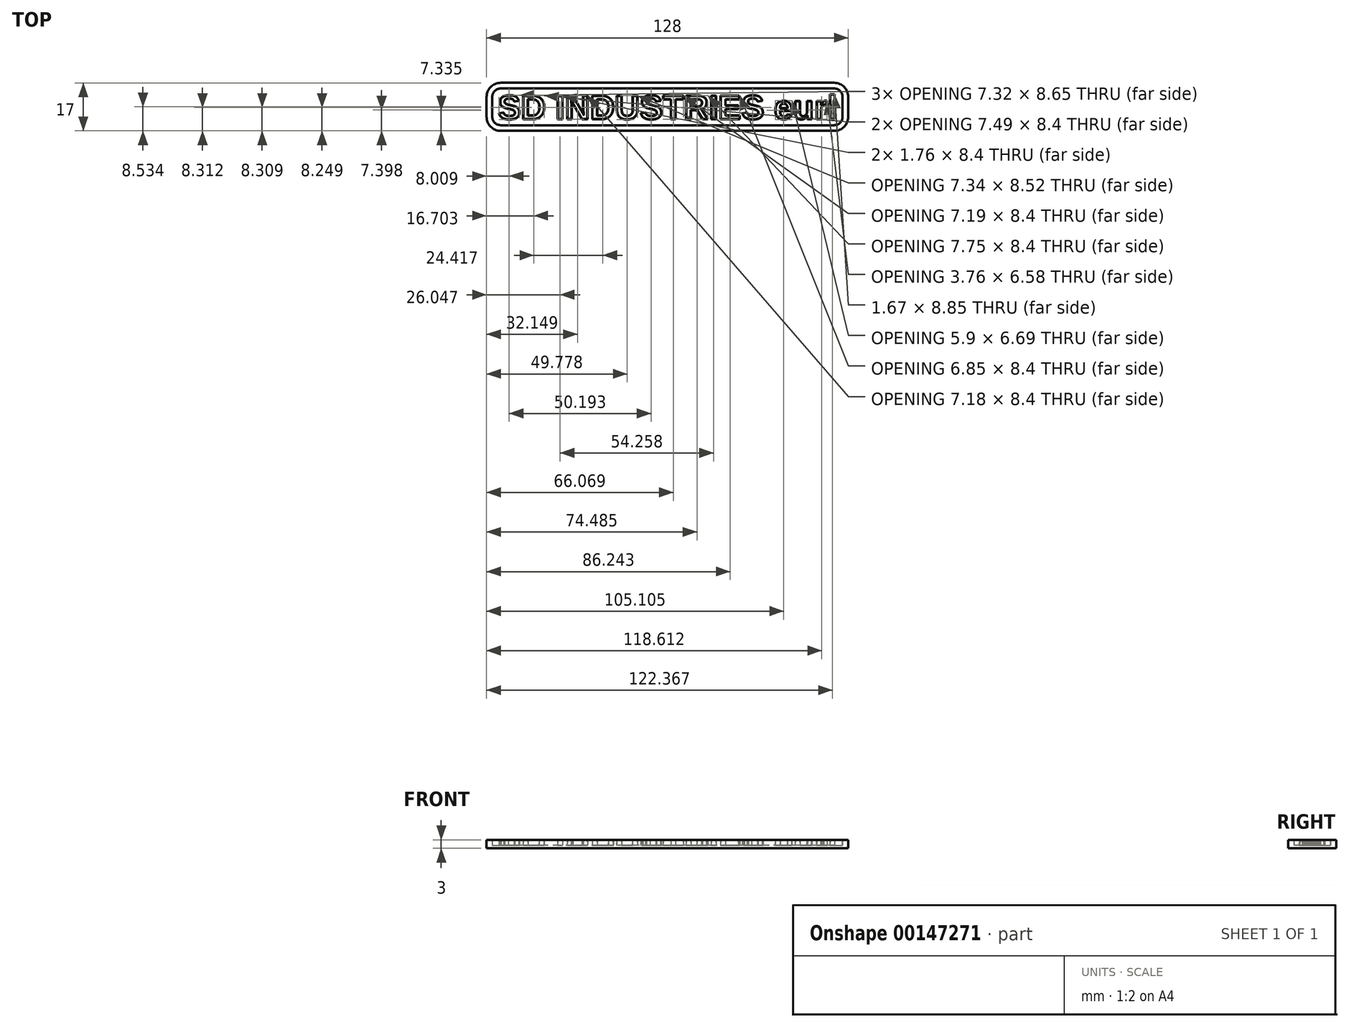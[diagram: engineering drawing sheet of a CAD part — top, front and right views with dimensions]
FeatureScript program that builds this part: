
annotation { "Feature Type Name" : "Feature", "Feature Type Description" : "" }
export const myFeature = defineFeature(function(context is Context, id is Id, definition is map)
    precondition{}
    {
        {
            var Q0;
            Q0=qCreatedBy(makeId("Top.planeOp"),FACE);
            var sketch = newSketch(context, id + "F0", { "sketchPlane" : qUnion([Q0])});
            skText(sketch, "E0", { "text": "SD INDUSTRIES eurl", "fontName": "Arimo-Bold.ttf"});
            skLineSegment(sketch, "E1.bottom", {"start": v(59, -2.1) * mm, "end": v(-59, -2.1) * mm});
            skLineSegment(sketch, "E1.top", {"start": v(59, 10.9) * mm, "end": v(-59, 10.9) * mm});
            skLineSegment(sketch, "E1.left", {"start": v(62, 0.9) * mm, "end": v(62, 7.9) * mm});
            skLineSegment(sketch, "E1.right", {"start": v(-62, 0.9) * mm, "end": v(-62, 7.9) * mm});
            skPoint(sketch, "E1.middle", {"position": v(0, 4.4) * mm});
            skPoint(sketch, "E2.visualSharp", {"position": v(-62, 10.9) * mm});
            skArc(sketch, "E2.filletArc", {"start": v(-59, 10.9) * mm, "mid": v(-61.12, 10.01) * mm, "end": v(-62, 7.9) * mm});
            skPoint(sketch, "E3.visualSharp", {"position": v(-62, -2.1) * mm});
            skArc(sketch, "E3.filletArc", {"start": v(-62, 0.9) * mm, "mid": v(-61.12, -1.23) * mm, "end": v(-59, -2.1) * mm});
            skPoint(sketch, "E4.visualSharp", {"position": v(62, -2.1) * mm});
            skArc(sketch, "E4.filletArc", {"start": v(59, -2.1) * mm, "mid": v(61.12, -1.23) * mm, "end": v(62, 0.9) * mm});
            skPoint(sketch, "E5.visualSharp", {"position": v(62, 10.9) * mm});
            skArc(sketch, "E5.filletArc", {"start": v(62, 7.9) * mm, "mid": v(61.12, 10.01) * mm, "end": v(59, 10.9) * mm});
            skArc(sketch, "E6.0", {"start": v(64, 7.9) * mm, "mid": v(62.54, 11.43) * mm, "end": v(59, 12.9) * mm});
            skLineSegment(sketch, "E6.1", {"start": v(64, 0.9) * mm, "end": v(64, 7.9) * mm});
            skLineSegment(sketch, "E6.2", {"start": v(59, 12.9) * mm, "end": v(-59, 12.9) * mm});
            skArc(sketch, "E6.3", {"start": v(59, -4.1) * mm, "mid": v(62.54, -2.64) * mm, "end": v(64, 0.9) * mm});
            skArc(sketch, "E6.4", {"start": v(-59, 12.9) * mm, "mid": v(-62.54, 11.43) * mm, "end": v(-64, 7.9) * mm});
            skLineSegment(sketch, "E6.5", {"start": v(-64, 0.9) * mm, "end": v(-64, 7.9) * mm});
            skArc(sketch, "E6.6", {"start": v(-64, 0.9) * mm, "mid": v(-62.54, -2.64) * mm, "end": v(-59, -4.1) * mm});
            skLineSegment(sketch, "E6.7", {"start": v(59, -4.1) * mm, "end": v(-59, -4.1) * mm});
            const initialGuessF0  = {"E0": [-0.06, 0, 1, 0, 0.00879]};
            skSetInitialGuess(sketch, initialGuessF0);
            skSolve(sketch);
        }
        {
            var Q0;
            Q0=qCreatedBy(makeId("Top.planeOp"),FACE);
            var sketch = newSketch(context, id + "F1", { "sketchPlane" : qUnion([Q0])});
            skLineSegment(sketch, "E7.0", {"start": v(59, 12.9) * mm, "end": v(-59, 12.9) * mm});
            skArc(sketch, "E8.0", {"start": v(-59, 12.9) * mm, "mid": v(-62.54, 11.43) * mm, "end": v(-64, 7.9) * mm});
            skLineSegment(sketch, "E9.0", {"start": v(-64, 0.9) * mm, "end": v(-64, 7.9) * mm});
            skArc(sketch, "E10.0", {"start": v(-64, 0.9) * mm, "mid": v(-62.54, -2.64) * mm, "end": v(-59, -4.1) * mm});
            skLineSegment(sketch, "E11.0", {"start": v(59, -4.1) * mm, "end": v(-59, -4.1) * mm});
            skArc(sketch, "E12.0", {"start": v(59, -4.1) * mm, "mid": v(62.54, -2.64) * mm, "end": v(64, 0.9) * mm});
            skLineSegment(sketch, "E13.0", {"start": v(64, 0.9) * mm, "end": v(64, 7.9) * mm});
            skArc(sketch, "E14.0", {"start": v(64, 7.9) * mm, "mid": v(62.54, 11.43) * mm, "end": v(59, 12.9) * mm});
            skSolve(sketch);
        }
        {
            var Q0;
            Q0=makeQuery(id+"F0.imprint","IMPRINT",FACE,{"disambiguationData":[TD([[makeQuery(id+"F0.imprint","IMPRINT",EDGE,{"derivedFrom":sQuery(id+"F0.wireOp",EDGE,"E1.bottom")}),1.0]])]});
            var Q1;
            Q1=makeQuery(id+"F0.imprint","IMPRINT",FACE,{"disambiguationData":[TD([[makeQuery(id+"F0.imprint","IMPRINT",EDGE,{"derivedFrom":sQuery(id+"F0.wireOp",EDGE,"E0.sketch_text.stroke-50")}),-1.0]])]});
            var Q2;
            Q2=makeQuery(id+"F0.imprint","IMPRINT",FACE,{"disambiguationData":[TD([[makeQuery(id+"F0.imprint","IMPRINT",EDGE,{"derivedFrom":sQuery(id+"F0.wireOp",EDGE,"E0.sketch_text.stroke-46")}),-1.0]])]});
            var Q3;
            Q3=makeQuery(id+"F0.imprint","IMPRINT",FACE,{"disambiguationData":[TD([[makeQuery(id+"F0.imprint","IMPRINT",EDGE,{"derivedFrom":sQuery(id+"F0.wireOp",EDGE,"E0.sketch_text.stroke-0")}),-1.0]])]});
            var Q4;
            Q4=makeQuery(id+"F0.imprint","IMPRINT",FACE,{"disambiguationData":[TD([[makeQuery(id+"F0.imprint","IMPRINT",EDGE,{"derivedFrom":sQuery(id+"F0.wireOp",EDGE,"E0.sketch_text.stroke-31")}),-1.0]])]});
            var Q5;
            Q5=makeQuery(id+"F0.imprint","IMPRINT",FACE,{"disambiguationData":[TD([[makeQuery(id+"F0.imprint","IMPRINT",EDGE,{"derivedFrom":sQuery(id+"F0.wireOp",EDGE,"E0.sketch_text.stroke-195")}),-1.0]])]});
            var Q6;
            Q6=makeQuery(id+"F0.imprint","IMPRINT",FACE,{"disambiguationData":[TD([[makeQuery(id+"F0.imprint","IMPRINT",EDGE,{"derivedFrom":sQuery(id+"F0.wireOp",EDGE,"E0.sketch_text.stroke-130")}),-1.0]])]});
            var Q7;
            Q7=makeQuery(id+"F0.imprint","IMPRINT",FACE,{"disambiguationData":[TD([[makeQuery(id+"F0.imprint","IMPRINT",EDGE,{"derivedFrom":sQuery(id+"F0.wireOp",EDGE,"E0.sketch_text.stroke-62")}),-1.0]])]});
            var Q8;
            Q8=makeQuery(id+"F0.imprint","IMPRINT",FACE,{"disambiguationData":[TD([[makeQuery(id+"F0.imprint","IMPRINT",EDGE,{"derivedFrom":sQuery(id+"F0.wireOp",EDGE,"E0.sketch_text.stroke-77")}),-1.0]])]});
            var Q9;
            Q9=makeQuery(id+"F0.imprint","IMPRINT",FACE,{"disambiguationData":[TD([[makeQuery(id+"F0.imprint","IMPRINT",EDGE,{"derivedFrom":sQuery(id+"F0.wireOp",EDGE,"E0.sketch_text.stroke-91")}),-1.0]])]});
            var Q10;
            Q10=makeQuery(id+"F0.imprint","IMPRINT",FACE,{"disambiguationData":[TD([[makeQuery(id+"F0.imprint","IMPRINT",EDGE,{"derivedFrom":sQuery(id+"F0.wireOp",EDGE,"E0.sketch_text.stroke-122")}),-1.0]])]});
            var Q11;
            Q11=makeQuery(id+"F0.imprint","IMPRINT",FACE,{"disambiguationData":[TD([[makeQuery(id+"F0.imprint","IMPRINT",EDGE,{"derivedFrom":sQuery(id+"F0.wireOp",EDGE,"E0.sketch_text.stroke-148")}),-1.0]])]});
            var Q12;
            Q12=makeQuery(id+"F0.imprint","IMPRINT",FACE,{"disambiguationData":[TD([[makeQuery(id+"F0.imprint","IMPRINT",EDGE,{"derivedFrom":sQuery(id+"F0.wireOp",EDGE,"E0.sketch_text.stroke-152")}),-1.0]])]});
            var Q13;
            Q13=makeQuery(id+"F0.imprint","IMPRINT",FACE,{"disambiguationData":[TD([[makeQuery(id+"F0.imprint","IMPRINT",EDGE,{"derivedFrom":sQuery(id+"F0.wireOp",EDGE,"E0.sketch_text.stroke-164")}),-1.0]])]});
            var Q14;
            Q14=makeQuery(id+"F0.imprint","IMPRINT",FACE,{"disambiguationData":[TD([[makeQuery(id+"F0.imprint","IMPRINT",EDGE,{"derivedFrom":sQuery(id+"F0.wireOp",EDGE,"E0.sketch_text.stroke-230")}),-1.0]])]});
            var Q15;
            Q15=makeQuery(id+"F0.imprint","IMPRINT",FACE,{"disambiguationData":[TD([[makeQuery(id+"F0.imprint","IMPRINT",EDGE,{"derivedFrom":sQuery(id+"F0.wireOp",EDGE,"E0.sketch_text.stroke-213")}),-1.0]])]});
            var Q16;
            Q16=makeQuery(id+"F0.imprint","IMPRINT",FACE,{"disambiguationData":[TD([[makeQuery(id+"F0.imprint","IMPRINT",EDGE,{"derivedFrom":sQuery(id+"F0.wireOp",EDGE,"E0.sketch_text.stroke-247")}),-1.0]])]});
            var Q17;
            Q17 = qSketchRegion(id + "F0", true);
            extrude(context, id + "F2", {"entities" : qUnion([Q0, Q1, Q2, Q3, Q4, Q5, Q6, Q7, Q8, Q9, Q10, Q11, Q12, Q13, Q14, Q15, Q16, Q17]), "depth" : 3 * mm});
        }
        {
            var Q0;
            Q0 = qSketchRegion(id + "F1", true);
            extrude(context, id + "F3", {"entities" : qUnion([Q0]), "operationType" : NewBodyOperationType.ADD, "depth" : 1 * mm});
        }
        {
            var Q0;
            Q0=makeQuery(id+"F3.boolean.opBoolean","SPLIT",FACE,{"disambiguationData":[TD([makeQuery(id+"F2.opExtrude","SWEPT_FACE",FACE,{"disambiguationData":[OSD([sQuery(id+"F0.wireOp",EDGE,"E0.sketch_text.stroke-0")])]})])],"derivedFrom":makeQuery(id+"F3.opExtrude","CAP_FACE",FACE,{"disambiguationData":[OSD([sQuery(id+"F1.wireOp",EDGE,"E7.0"),sQuery(id+"F1.wireOp",EDGE,"E8.0"),sQuery(id+"F1.wireOp",EDGE,"E9.0"),sQuery(id+"F1.wireOp",EDGE,"E10.0"),sQuery(id+"F1.wireOp",EDGE,"E11.0"),sQuery(id+"F1.wireOp",EDGE,"E12.0"),sQuery(id+"F1.wireOp",EDGE,"E13.0"),sQuery(id+"F1.wireOp",EDGE,"E14.0")])],"isStart":false})});
            var Q1;
            Q1=makeQuery(id+"F3.boolean.opBoolean","SPLIT",FACE,{"disambiguationData":[TD([makeQuery(id+"F2.opExtrude","SWEPT_FACE",FACE,{"disambiguationData":[OSD([sQuery(id+"F0.wireOp",EDGE,"E0.sketch_text.stroke-39")])]})])],"derivedFrom":makeQuery(id+"F3.opExtrude","CAP_FACE",FACE,{"disambiguationData":[OSD([sQuery(id+"F1.wireOp",EDGE,"E7.0"),sQuery(id+"F1.wireOp",EDGE,"E8.0"),sQuery(id+"F1.wireOp",EDGE,"E9.0"),sQuery(id+"F1.wireOp",EDGE,"E10.0"),sQuery(id+"F1.wireOp",EDGE,"E11.0"),sQuery(id+"F1.wireOp",EDGE,"E12.0"),sQuery(id+"F1.wireOp",EDGE,"E13.0"),sQuery(id+"F1.wireOp",EDGE,"E14.0")])],"isStart":false})});
            var Q2;
            Q2=makeQuery(id+"F3.boolean.opBoolean","SPLIT",FACE,{"disambiguationData":[TD([makeQuery(id+"F2.opExtrude","SWEPT_FACE",FACE,{"disambiguationData":[OSD([sQuery(id+"F0.wireOp",EDGE,"E0.sketch_text.stroke-70")])]})])],"derivedFrom":makeQuery(id+"F3.opExtrude","CAP_FACE",FACE,{"disambiguationData":[OSD([sQuery(id+"F1.wireOp",EDGE,"E7.0"),sQuery(id+"F1.wireOp",EDGE,"E8.0"),sQuery(id+"F1.wireOp",EDGE,"E9.0"),sQuery(id+"F1.wireOp",EDGE,"E10.0"),sQuery(id+"F1.wireOp",EDGE,"E11.0"),sQuery(id+"F1.wireOp",EDGE,"E12.0"),sQuery(id+"F1.wireOp",EDGE,"E13.0"),sQuery(id+"F1.wireOp",EDGE,"E14.0")])],"isStart":false})});
            var Q3;
            Q3=makeQuery(id+"F3.boolean.opBoolean","SPLIT",FACE,{"disambiguationData":[TD([makeQuery(id+"F2.opExtrude","SWEPT_FACE",FACE,{"disambiguationData":[OSD([sQuery(id+"F0.wireOp",EDGE,"E0.sketch_text.stroke-142")])]})])],"derivedFrom":makeQuery(id+"F3.opExtrude","CAP_FACE",FACE,{"disambiguationData":[OSD([sQuery(id+"F1.wireOp",EDGE,"E7.0"),sQuery(id+"F1.wireOp",EDGE,"E8.0"),sQuery(id+"F1.wireOp",EDGE,"E9.0"),sQuery(id+"F1.wireOp",EDGE,"E10.0"),sQuery(id+"F1.wireOp",EDGE,"E11.0"),sQuery(id+"F1.wireOp",EDGE,"E12.0"),sQuery(id+"F1.wireOp",EDGE,"E13.0"),sQuery(id+"F1.wireOp",EDGE,"E14.0")])],"isStart":false})});
            var Q4;
            Q4=makeQuery(id+"F3.boolean.opBoolean","SPLIT",FACE,{"disambiguationData":[TD([makeQuery(id+"F2.opExtrude","SWEPT_FACE",FACE,{"disambiguationData":[OSD([sQuery(id+"F0.wireOp",EDGE,"E0.sketch_text.stroke-208")])]})])],"derivedFrom":makeQuery(id+"F3.opExtrude","CAP_FACE",FACE,{"disambiguationData":[OSD([sQuery(id+"F1.wireOp",EDGE,"E7.0"),sQuery(id+"F1.wireOp",EDGE,"E8.0"),sQuery(id+"F1.wireOp",EDGE,"E9.0"),sQuery(id+"F1.wireOp",EDGE,"E10.0"),sQuery(id+"F1.wireOp",EDGE,"E11.0"),sQuery(id+"F1.wireOp",EDGE,"E12.0"),sQuery(id+"F1.wireOp",EDGE,"E13.0"),sQuery(id+"F1.wireOp",EDGE,"E14.0")])],"isStart":false})});
            extrude(context, id + "F4", {"entities" : qUnion([Q0, Q1, Q2, Q3, Q4]), "depth" : 2 * mm, "hasDraft" : true, "draftAngle" : 3 * degree});
        }
        {
            var Q0;
            Q0=makeQuery(id+"F4.opExtrude","CAP_EDGE",EDGE,{"disambiguationData":[OSD([sQuery(id+"F0.wireOp",EDGE,"E1.top"),sQuery(id+"F1.wireOp",EDGE,"E7.0"),sQuery(id+"F1.wireOp",EDGE,"E8.0"),sQuery(id+"F1.wireOp",EDGE,"E9.0"),sQuery(id+"F1.wireOp",EDGE,"E10.0"),sQuery(id+"F1.wireOp",EDGE,"E11.0"),sQuery(id+"F1.wireOp",EDGE,"E12.0"),sQuery(id+"F1.wireOp",EDGE,"E13.0"),sQuery(id+"F1.wireOp",EDGE,"E14.0")])],"isStart":false});
            var Q1;
            Q1=makeQuery(id+"F4.opExtrude","CAP_EDGE",EDGE,{"disambiguationData":[OSD([sQuery(id+"F0.wireOp",EDGE,"E2.filletArc"),sQuery(id+"F1.wireOp",EDGE,"E7.0"),sQuery(id+"F1.wireOp",EDGE,"E8.0"),sQuery(id+"F1.wireOp",EDGE,"E9.0"),sQuery(id+"F1.wireOp",EDGE,"E10.0"),sQuery(id+"F1.wireOp",EDGE,"E11.0"),sQuery(id+"F1.wireOp",EDGE,"E12.0"),sQuery(id+"F1.wireOp",EDGE,"E13.0"),sQuery(id+"F1.wireOp",EDGE,"E14.0")])],"isStart":false});
            var Q2;
            Q2=makeQuery(id+"F4.opExtrude","CAP_EDGE",EDGE,{"disambiguationData":[OSD([sQuery(id+"F0.wireOp",EDGE,"E1.right"),sQuery(id+"F1.wireOp",EDGE,"E7.0"),sQuery(id+"F1.wireOp",EDGE,"E8.0"),sQuery(id+"F1.wireOp",EDGE,"E9.0"),sQuery(id+"F1.wireOp",EDGE,"E10.0"),sQuery(id+"F1.wireOp",EDGE,"E11.0"),sQuery(id+"F1.wireOp",EDGE,"E12.0"),sQuery(id+"F1.wireOp",EDGE,"E13.0"),sQuery(id+"F1.wireOp",EDGE,"E14.0")])],"isStart":false});
            var Q3;
            Q3=makeQuery(id+"F4.opExtrude","CAP_EDGE",EDGE,{"disambiguationData":[OSD([sQuery(id+"F0.wireOp",EDGE,"E3.filletArc"),sQuery(id+"F1.wireOp",EDGE,"E7.0"),sQuery(id+"F1.wireOp",EDGE,"E8.0"),sQuery(id+"F1.wireOp",EDGE,"E9.0"),sQuery(id+"F1.wireOp",EDGE,"E10.0"),sQuery(id+"F1.wireOp",EDGE,"E11.0"),sQuery(id+"F1.wireOp",EDGE,"E12.0"),sQuery(id+"F1.wireOp",EDGE,"E13.0"),sQuery(id+"F1.wireOp",EDGE,"E14.0")])],"isStart":false});
            var Q4;
            Q4=makeQuery(id+"F4.opExtrude","CAP_EDGE",EDGE,{"disambiguationData":[OSD([sQuery(id+"F0.wireOp",EDGE,"E1.bottom"),sQuery(id+"F1.wireOp",EDGE,"E7.0"),sQuery(id+"F1.wireOp",EDGE,"E8.0"),sQuery(id+"F1.wireOp",EDGE,"E9.0"),sQuery(id+"F1.wireOp",EDGE,"E10.0"),sQuery(id+"F1.wireOp",EDGE,"E11.0"),sQuery(id+"F1.wireOp",EDGE,"E12.0"),sQuery(id+"F1.wireOp",EDGE,"E13.0"),sQuery(id+"F1.wireOp",EDGE,"E14.0")])],"isStart":false});
            var Q5;
            Q5=makeQuery(id+"F4.opExtrude","CAP_EDGE",EDGE,{"disambiguationData":[OSD([sQuery(id+"F0.wireOp",EDGE,"E5.filletArc"),sQuery(id+"F1.wireOp",EDGE,"E7.0"),sQuery(id+"F1.wireOp",EDGE,"E8.0"),sQuery(id+"F1.wireOp",EDGE,"E9.0"),sQuery(id+"F1.wireOp",EDGE,"E10.0"),sQuery(id+"F1.wireOp",EDGE,"E11.0"),sQuery(id+"F1.wireOp",EDGE,"E12.0"),sQuery(id+"F1.wireOp",EDGE,"E13.0"),sQuery(id+"F1.wireOp",EDGE,"E14.0")])],"isStart":false});
            var Q6;
            Q6=makeQuery(id+"F4.opExtrude","CAP_EDGE",EDGE,{"disambiguationData":[OSD([sQuery(id+"F0.wireOp",EDGE,"E1.left"),sQuery(id+"F1.wireOp",EDGE,"E7.0"),sQuery(id+"F1.wireOp",EDGE,"E8.0"),sQuery(id+"F1.wireOp",EDGE,"E9.0"),sQuery(id+"F1.wireOp",EDGE,"E10.0"),sQuery(id+"F1.wireOp",EDGE,"E11.0"),sQuery(id+"F1.wireOp",EDGE,"E12.0"),sQuery(id+"F1.wireOp",EDGE,"E13.0"),sQuery(id+"F1.wireOp",EDGE,"E14.0")])],"isStart":false});
            var Q7;
            Q7=makeQuery(id+"F4.opExtrude","CAP_EDGE",EDGE,{"disambiguationData":[OSD([sQuery(id+"F0.wireOp",EDGE,"E4.filletArc"),sQuery(id+"F1.wireOp",EDGE,"E7.0"),sQuery(id+"F1.wireOp",EDGE,"E8.0"),sQuery(id+"F1.wireOp",EDGE,"E9.0"),sQuery(id+"F1.wireOp",EDGE,"E10.0"),sQuery(id+"F1.wireOp",EDGE,"E11.0"),sQuery(id+"F1.wireOp",EDGE,"E12.0"),sQuery(id+"F1.wireOp",EDGE,"E13.0"),sQuery(id+"F1.wireOp",EDGE,"E14.0")])],"isStart":false});
            chamfer(context, id + "F5", {"entities" : qUnion([Q0, Q1, Q2, Q3, Q4, Q5, Q6, Q7]), "chamferType" : ChamferType.OFFSET_ANGLE, "width" : 2 * mm, "oppositeDirection" : true, "angle" : 3 * degree, "tangentPropagation" : true});
        }
    });
